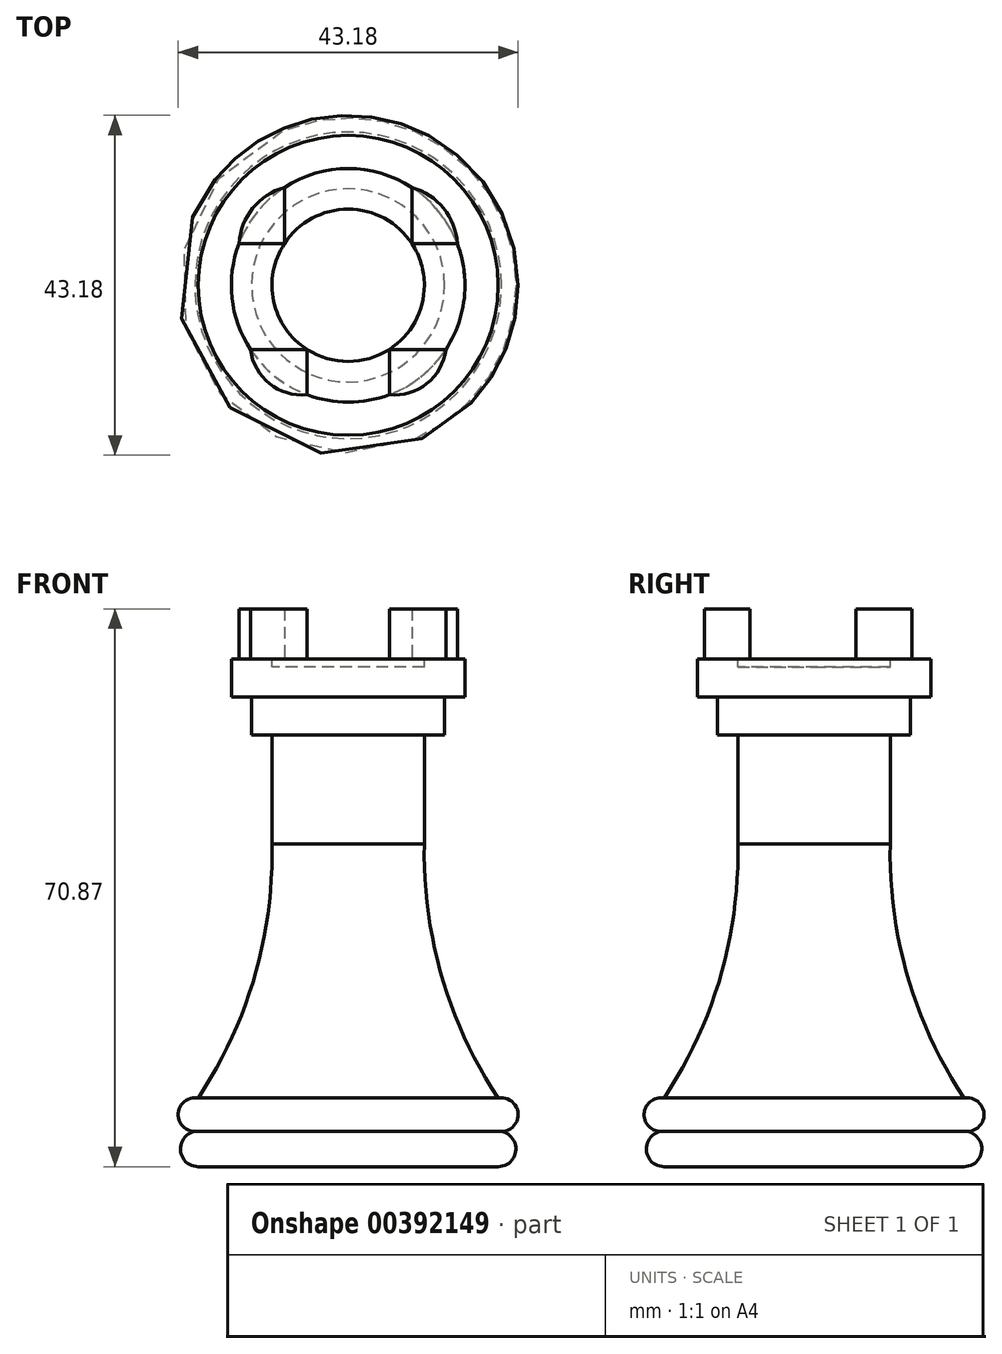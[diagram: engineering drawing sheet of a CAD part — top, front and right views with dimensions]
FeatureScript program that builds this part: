
annotation { "Feature Type Name" : "Feature", "Feature Type Description" : "" }
export const myFeature = defineFeature(function(context is Context, id is Id, definition is map)
    precondition{}
    {
        {
            var Q0;
            Q0=qCreatedBy(makeId("Front.planeOp"),FACE);
            var sketch = newSketch(context, id + "F0", { "sketchPlane" : qUnion([Q0])});
            skLineSegment(sketch, "E0", {"start": v(0, 22.53) * mm, "end": v(0, -40.97) * mm});
            skLineSegment(sketch, "E1", {"start": v(0, -40.97) * mm, "end": v(-19.05, -40.97) * mm});
            skArc(sketch, "E2", {"start": v(-19.05, -36.46) * mm, "mid": v(-21.3, -38.71) * mm, "end": v(-19.05, -40.97) * mm});
            skArc(sketch, "E3", {"start": v(-19.05, -32.26) * mm, "mid": v(-21.6, -34.36) * mm, "end": v(-19.05, -36.46) * mm});
            skArc(sketch, "E4", {"start": v(-19.05, -32.26) * mm, "mid": v(-11.9, -16.85) * mm, "end": v(-9.68, 0) * mm});
            skLineSegment(sketch, "E5", {"start": v(-9.68, 0) * mm, "end": v(-9.68, 13.87) * mm});
            skLineSegment(sketch, "E6", {"start": v(-12.26, 18.71) * mm, "end": v(-14.84, 18.71) * mm});
            skLineSegment(sketch, "E7", {"start": v(-14.84, 18.71) * mm, "end": v(-14.84, 23.55) * mm});
            skLineSegment(sketch, "E8", {"start": v(-14.84, 23.55) * mm, "end": v(-9.68, 23.55) * mm});
            skLineSegment(sketch, "E9", {"start": v(0, 23.55) * mm, "end": v(0, -40.97) * mm});
            skLineSegment(sketch, "E10.top", {"start": v(-9.68, 22.53) * mm, "end": v(0, 22.53) * mm});
            skLineSegment(sketch, "E10.left", {"start": v(-9.68, 23.55) * mm, "end": v(-9.68, 22.53) * mm});
            skLineSegment(sketch, "E10.right", {"start": v(0, 23.55) * mm, "end": v(0, 22.53) * mm});
            skLineSegment(sketch, "E11.bottom", {"start": v(-9.68, 13.87) * mm, "end": v(-12.26, 13.87) * mm});
            skLineSegment(sketch, "E11.top", {"start": v(-9.68, 18.71) * mm, "end": v(-12.26, 18.71) * mm});
            skLineSegment(sketch, "E11.right", {"start": v(-12.26, 13.87) * mm, "end": v(-12.26, 18.71) * mm});
            skPoint(sketch, "E12.orphan", {"position": v(-9.68, 18.71) * mm});
            skSolve(sketch);
        }
        {
            var Q0;
            Q0=qSketchRegion(id+"F0",true);
            var Q1;
            Q1=sQuery(id+"F0.wireOp",EDGE,"E9");
            revolve(context, id + "F1", {"entities" : qUnion([Q0]), "axis" : qUnion([Q1]), "revolveType" : RevolveType.FULL});
        }
        {
            var Q0;
            Q0=makeQuery(id+"F1.opRevolve","SWEPT_FACE",FACE,{"disambiguationData":[OSD([sQuery(id+"F0.wireOp",EDGE,"E8")])]});
            var sketch = newSketch(context, id + "F2", { "sketchPlane" : qUnion([Q0])});
            skLineSegment(sketch, "E13", {"start": v(-13.87, 5.29) * mm, "end": v(-8.1, 5.29) * mm});
            skLineSegment(sketch, "E14", {"start": v(-8.1, 5.29) * mm, "end": v(-8.1, 12.43) * mm});
            skArc(sketch, "E15", {"start": v(-8.1, 12.43) * mm, "mid": v(-12.12, 9.78) * mm, "end": v(-13.87, 5.29) * mm});
            skLineSegment(sketch, "E16", {"start": v(0, 27.42) * mm, "end": v(0, -30.33) * mm});
            skArc(sketch, "E17.MirrorCS", {"start": v(8.1, 12.43) * mm, "mid": v(12.12, 9.78) * mm, "end": v(13.87, 5.29) * mm});
            skLineSegment(sketch, "E18.MirrorCS", {"start": v(8.1, 5.29) * mm, "end": v(8.1, 12.43) * mm});
            skLineSegment(sketch, "E19.MirrorCS", {"start": v(13.87, 5.29) * mm, "end": v(8.1, 5.29) * mm});
            skLineSegment(sketch, "E20", {"start": v(-12.4, -8.15) * mm, "end": v(-5.22, -8.15) * mm});
            skLineSegment(sketch, "E21", {"start": v(-5.22, -8.15) * mm, "end": v(-5.22, -13.9) * mm});
            skArc(sketch, "E22", {"start": v(-12.4, -8.15) * mm, "mid": v(-9.99, -12.48) * mm, "end": v(-5.22, -13.9) * mm});
            skLineSegment(sketch, "E23.MirrorCS", {"start": v(12.4, -8.15) * mm, "end": v(5.22, -8.15) * mm});
            skLineSegment(sketch, "E24.MirrorCS", {"start": v(5.22, -8.15) * mm, "end": v(5.22, -13.9) * mm});
            skArc(sketch, "E25.MirrorCS", {"start": v(12.4, -8.15) * mm, "mid": v(9.99, -12.48) * mm, "end": v(5.22, -13.9) * mm});
            skPoint(sketch, "E26.MirrorCS.end.orphan", {"position": v(-5.22, -2.4) * mm});
            skPoint(sketch, "E26.MirrorCS.start.orphan", {"position": v(-5.22, -8.15) * mm});
            skSolve(sketch);
        }
        {
            var Q0;
            Q0=qSketchRegion(id+"F2",true);
            extrude(context, id + "F3", {"entities" : qUnion([Q0]), "operationType" : NewBodyOperationType.ADD, "depth" : 6.35 * mm});
        }
    });
